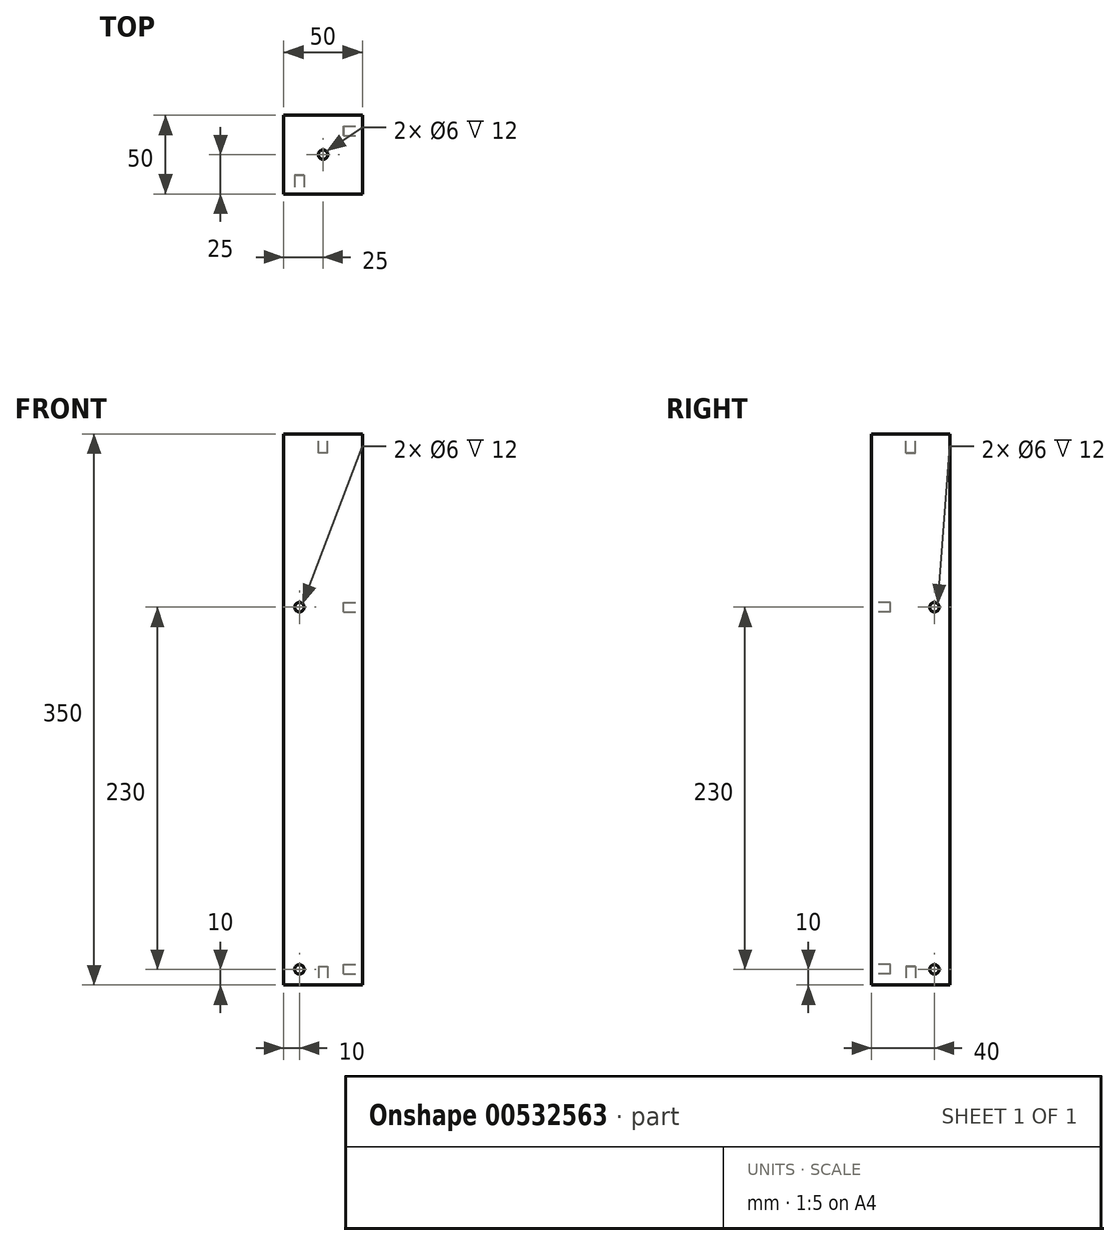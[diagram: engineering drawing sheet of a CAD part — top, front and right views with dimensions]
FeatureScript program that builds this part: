
annotation { "Feature Type Name" : "Feature", "Feature Type Description" : "" }
export const myFeature = defineFeature(function(context is Context, id is Id, definition is map)
    precondition{}
    {
        {
            var Q0;
            Q0=qCreatedBy(makeId("Top.planeOp"),FACE);
            var sketch = newSketch(context, id + "F0", { "sketchPlane" : qUnion([Q0])});
            skLineSegment(sketch, "E0.bottom", {"start": v(0, 0) * mm, "end": v(50, 0) * mm});
            skLineSegment(sketch, "E0.top", {"start": v(0, 50) * mm, "end": v(50, 50) * mm});
            skLineSegment(sketch, "E0.left", {"start": v(0, 0) * mm, "end": v(0, 50) * mm});
            skLineSegment(sketch, "E0.right", {"start": v(50, 0) * mm, "end": v(50, 50) * mm});
            skSolve(sketch);
        }
        {
            var Q0;
            Q0 = qSketchRegion(id + "F0", true);
            extrude(context, id + "F1", {"entities" : qUnion([Q0]), "depth" : 350 * mm, "offsetDistance" : 25 * mm});
        }
        {
            var Q0;
            Q0=makeQuery(id+"F1.opExtrude","CAP_FACE",FACE,{"disambiguationData":[OSD([sQuery(id+"F0.wireOp",EDGE,"E0.bottom"),sQuery(id+"F0.wireOp",EDGE,"E0.top"),sQuery(id+"F0.wireOp",EDGE,"E0.left"),sQuery(id+"F0.wireOp",EDGE,"E0.right")])],"isStart":false});
            var sketch = newSketch(context, id + "F2", { "sketchPlane" : qUnion([Q0])});
            skCircle(sketch, "E1", {"center": v(25, 25) * mm, "radius": 3 * mm});
            skPoint(sketch, "E1.centerSnap0", {"position": v(0, 25) * mm});
            skSolve(sketch);
        }
        {
            var Q0;
            Q0 = qSketchRegion(id + "F2", true);
            extrude(context, id + "F3", {"entities" : qUnion([Q0]), "operationType" : NewBodyOperationType.REMOVE, "oppositeDirection" : true, "depth" : 12 * mm, "offsetDistance" : 25 * mm});
        }
        {
            var Q0;
            Q0=makeQuery(id+"F1.opExtrude","SWEPT_FACE",FACE,{"disambiguationData":[OSD([sQuery(id+"F0.wireOp",EDGE,"E0.bottom")])]});
            var sketch = newSketch(context, id + "F4", { "sketchPlane" : qUnion([Q0])});
            skCircle(sketch, "E2", {"center": v(10, 240) * mm, "radius": 3 * mm});
            skCircle(sketch, "E3", {"center": v(10, 10) * mm, "radius": 3 * mm});
            skSolve(sketch);
        }
        {
            var Q0;
            Q0 = qSketchRegion(id + "F4", true);
            extrude(context, id + "F5", {"entities" : qUnion([Q0]), "operationType" : NewBodyOperationType.REMOVE, "oppositeDirection" : true, "depth" : 12 * mm, "offsetDistance" : 25 * mm});
        }
        {
            var Q0;
            Q0=makeQuery(id+"F1.opExtrude","SWEPT_FACE",FACE,{"disambiguationData":[OSD([sQuery(id+"F0.wireOp",EDGE,"E0.right")])]});
            var sketch = newSketch(context, id + "F6", { "sketchPlane" : qUnion([Q0])});
            skCircle(sketch, "E4", {"center": v(40, 240) * mm, "radius": 3 * mm});
            skCircle(sketch, "E5", {"center": v(40, 10) * mm, "radius": 3 * mm});
            skSolve(sketch);
        }
        {
            var Q0;
            Q0 = qSketchRegion(id + "F6", true);
            extrude(context, id + "F7", {"entities" : qUnion([Q0]), "operationType" : NewBodyOperationType.REMOVE, "oppositeDirection" : true, "depth" : 12 * mm, "offsetDistance" : 25 * mm});
        }
        {
            var Q0;
            Q0=makeQuery(id+"F1.opExtrude","CAP_FACE",FACE,{"disambiguationData":[OSD([sQuery(id+"F0.wireOp",EDGE,"E0.bottom"),sQuery(id+"F0.wireOp",EDGE,"E0.top"),sQuery(id+"F0.wireOp",EDGE,"E0.left"),sQuery(id+"F0.wireOp",EDGE,"E0.right")])],"isStart":true});
            var sketch = newSketch(context, id + "F8", { "sketchPlane" : qUnion([Q0])});
            skCircle(sketch, "E6", {"center": v(25, -25) * mm, "radius": 3 * mm});
            skSolve(sketch);
        }
        {
            var Q0;
            Q0 = qSketchRegion(id + "F8", true);
            extrude(context, id + "F9", {"entities" : qUnion([Q0]), "operationType" : NewBodyOperationType.REMOVE, "oppositeDirection" : true, "depth" : 12 * mm, "offsetDistance" : 25 * mm});
        }
    });
